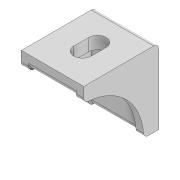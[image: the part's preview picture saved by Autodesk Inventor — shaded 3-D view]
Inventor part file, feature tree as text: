
AUTODESK INVENTOR PART (.ipt)
format: ipt  version: 2020 (Build 240168000, 168)  size: 164,864 bytes
history: native  units: mm
features: extrude x6, sketch x6, projected_geometry x2, other x1, fillet x1
ambient origin geometry x8: Origin, YZ Plane, XZ Plane, XY Plane, X Axis, Y Axis, Z Axis, Center Point
bodies: Body1 (feature_tree)
feature tree (16):
  other  "솔리드1"
  extrude  "돌출1"  Depth=25.0mm
  extrude  "돌출2"  Depth=30.0mm
  extrude  "돌출3"  Depth=5.0mm TaperAngle=0.0deg
  extrude  "돌출4"  Depth=5.0mm
  extrude  "돌출5"  Depth=25.0mm TaperAngle=0.0deg
  extrude  "돌출6"  Depth=3.0mm
  fillet  "모깎기1"  Radius=7.0mm
  sketch  "스케치1"
  sketch  "스케치2"
  sketch  "스케치3"
  sketch  "스케치4"
  sketch  "스케치5"
  projected_geometry  "투영된 루프1"
  sketch  "스케치6"
  projected_geometry  "투영된 루프2"
